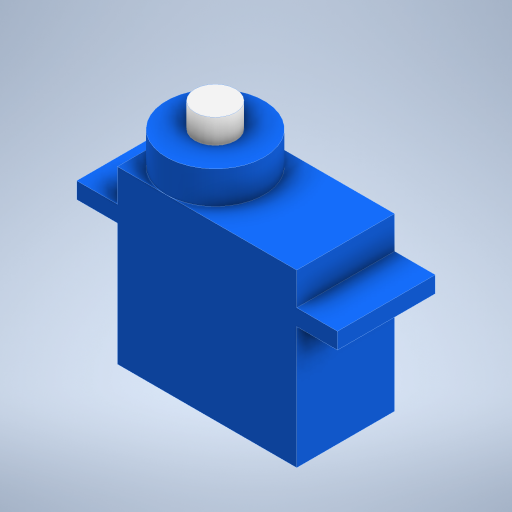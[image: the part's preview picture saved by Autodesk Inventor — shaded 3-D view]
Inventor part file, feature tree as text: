
AUTODESK INVENTOR PART (.ipt)
format: ipt  version: 2024.2 (Build 282272000, 272)  size: 283,648 bytes
history: native  units: mm
features: extrude x5, sketch x5, projected_geometry x1
ambient origin geometry x8: Origin, YZ Plane, XZ Plane, XY Plane, X Axis, Y Axis, Z Axis, Center Point
bodies: Solid1 (feature_tree)
feature tree (11):
  extrude  "Extrusion1"  Depth=12.0mm
  extrude  "Extrusion2"  Depth=5.0mm
  extrude  "Extrusion3"  Depth=2.0mm TaperAngle=0.0deg
  extrude  "Extrusion4"  Depth=12.0mm
  extrude  "Extrusion5"  Depth=5.0mm
  sketch  "Sketch1"  dims[d0=22.0mm d1=12.0mm]
  sketch  "Sketch2"  dims[d2=15.0mm d3=0.0mm d4=5.0mm]
  sketch  "Sketch3"  dims[d5=5.0mm d6=2.0mm d7=0.0mm]
  sketch  "Sketch4"  dims[d8=4.0mm d9=0.0mm d10=12.0mm]
  sketch  "Sketch5"  dims[d11=4.0mm d12=0.0mm d13=5.0mm d14=3.0mm d15=0.0mm]
  projected_geometry  "Projected Loop1"
